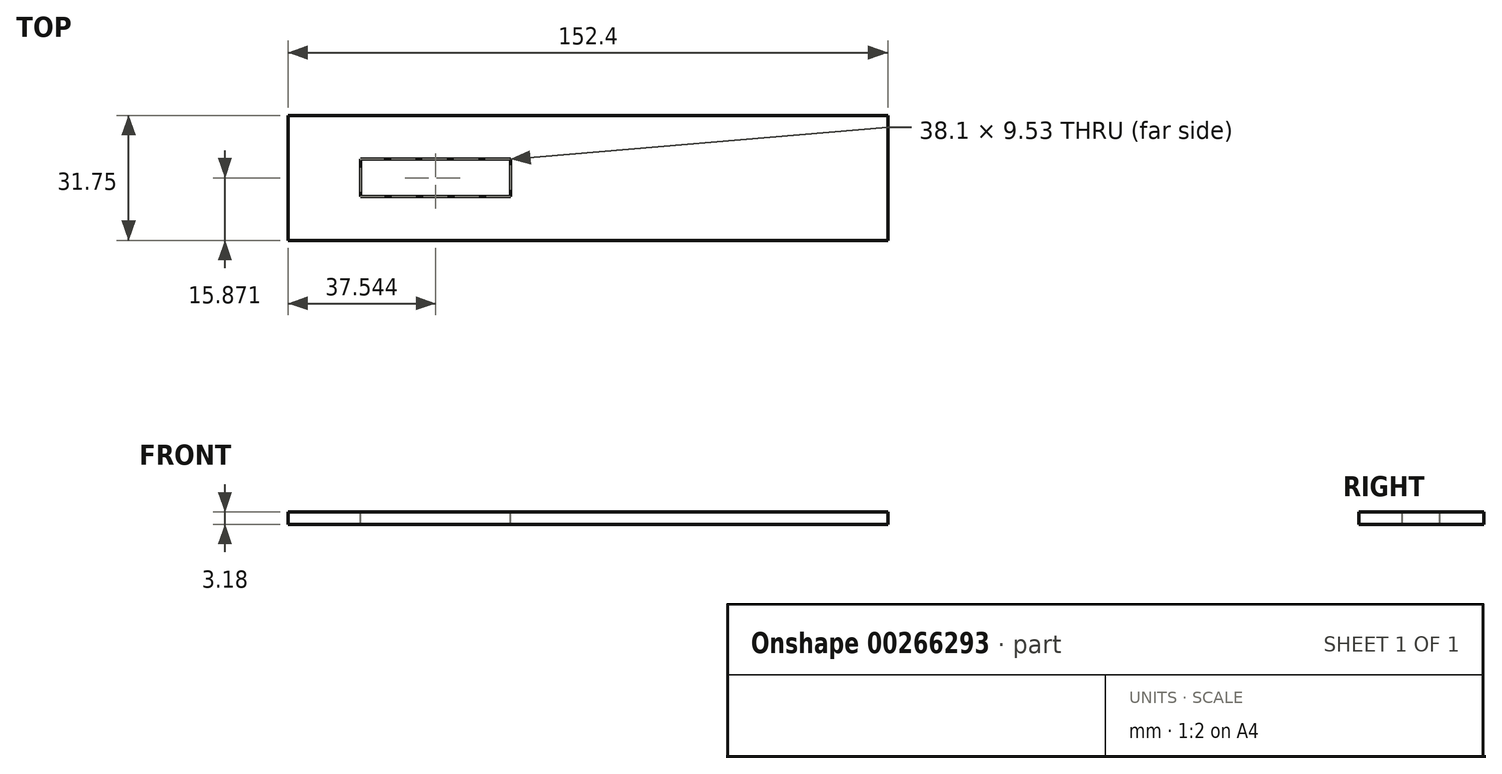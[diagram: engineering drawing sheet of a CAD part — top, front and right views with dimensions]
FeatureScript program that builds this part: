
annotation { "Feature Type Name" : "Feature", "Feature Type Description" : "" }
export const myFeature = defineFeature(function(context is Context, id is Id, definition is map)
    precondition{}
    {
        {
            var Q0;
            Q0=qCreatedBy(makeId("Top.planeOp"),FACE);
            var sketch = newSketch(context, id + "F0", { "sketchPlane" : qUnion([Q0])});
            skLineSegment(sketch, "E0.bottom", {"start": v(1.12, 23.06) * mm, "end": v(153.52, 23.06) * mm});
            skLineSegment(sketch, "E0.top", {"start": v(1.12, -8.7) * mm, "end": v(153.52, -8.7) * mm});
            skLineSegment(sketch, "E0.left", {"start": v(1.12, 23.06) * mm, "end": v(1.12, -8.7) * mm});
            skLineSegment(sketch, "E0.right", {"start": v(153.52, 23.06) * mm, "end": v(153.52, -8.7) * mm});
            skLineSegment(sketch, "E1.bottom", {"start": v(1.12, 8.32) * mm, "end": v(153.52, 8.32) * mm});
            skLineSegment(sketch, "E1.top", {"start": v(1.12, 0) * mm, "end": v(153.52, 0) * mm});
            skLineSegment(sketch, "E1.left", {"start": v(1.12, 8.32) * mm, "end": v(1.12, 0) * mm});
            skLineSegment(sketch, "E1.right", {"start": v(153.52, 8.32) * mm, "end": v(153.52, 0) * mm});
            skSolve(sketch);
        }
        {
            var Q0;
            Q0 = qSketchRegion(id + "F0", true);
            extrude(context, id + "F1", {"entities" : qUnion([Q0]), "depth" : 3.17 * mm});
        }
        {
            var Q0;
            Q0=makeQuery(id+"F0.imprint","IMPRINT",FACE,{"disambiguationData":[TD([[makeQuery(id+"F0.imprint","IMPRINT",EDGE,{"derivedFrom":sQuery(id+"F0.wireOp",EDGE,"E1.bottom")}),-1.0]])]});
            extrude(context, id + "F2", {"entities" : qUnion([Q0]), "operationType" : NewBodyOperationType.REMOVE, "oppositeDirection" : true, "depth" : 55.12 * mm});
        }
        {
            var Q0;
            Q0=makeQuery(id+"F1.opExtrude","CAP_FACE",FACE,{"disambiguationData":[OSD([sQuery(id+"F0.wireOp",EDGE,"E0.bottom"),sQuery(id+"F0.wireOp",EDGE,"E0.top"),sQuery(id+"F0.wireOp",EDGE,"E0.left"),sQuery(id+"F0.wireOp",EDGE,"E0.right"),sQuery(id+"F0.wireOp",EDGE,"E1.left"),sQuery(id+"F0.wireOp",EDGE,"E1.right")])],"isStart":false});
            var sketch = newSketch(context, id + "F3", { "sketchPlane" : qUnion([Q0])});
            skLineSegment(sketch, "E2.bottom", {"start": v(19.61, 11.94) * mm, "end": v(57.71, 11.94) * mm});
            skLineSegment(sketch, "E2.top", {"start": v(19.61, 2.42) * mm, "end": v(57.71, 2.42) * mm});
            skLineSegment(sketch, "E2.left", {"start": v(19.61, 11.94) * mm, "end": v(19.61, 2.42) * mm});
            skLineSegment(sketch, "E2.right", {"start": v(57.71, 11.94) * mm, "end": v(57.71, 2.42) * mm});
            skLineSegment(sketch, "E3", {"start": v(38.66, 11.94) * mm, "end": v(38.66, 2.42) * mm, "construction": true});
            skPoint(sketch, "E4", {"position": v(19.61, 7.18) * mm});
            skPoint(sketch, "E5", {"position": v(1.12, 7.18) * mm});
            skSolve(sketch);
        }
        {
            var Q0;
            Q0 = qSketchRegion(id + "F3", true);
            extrude(context, id + "F4", {"entities" : qUnion([Q0]), "operationType" : NewBodyOperationType.REMOVE, "oppositeDirection" : true, "depth" : 25.4 * mm});
        }
    });
